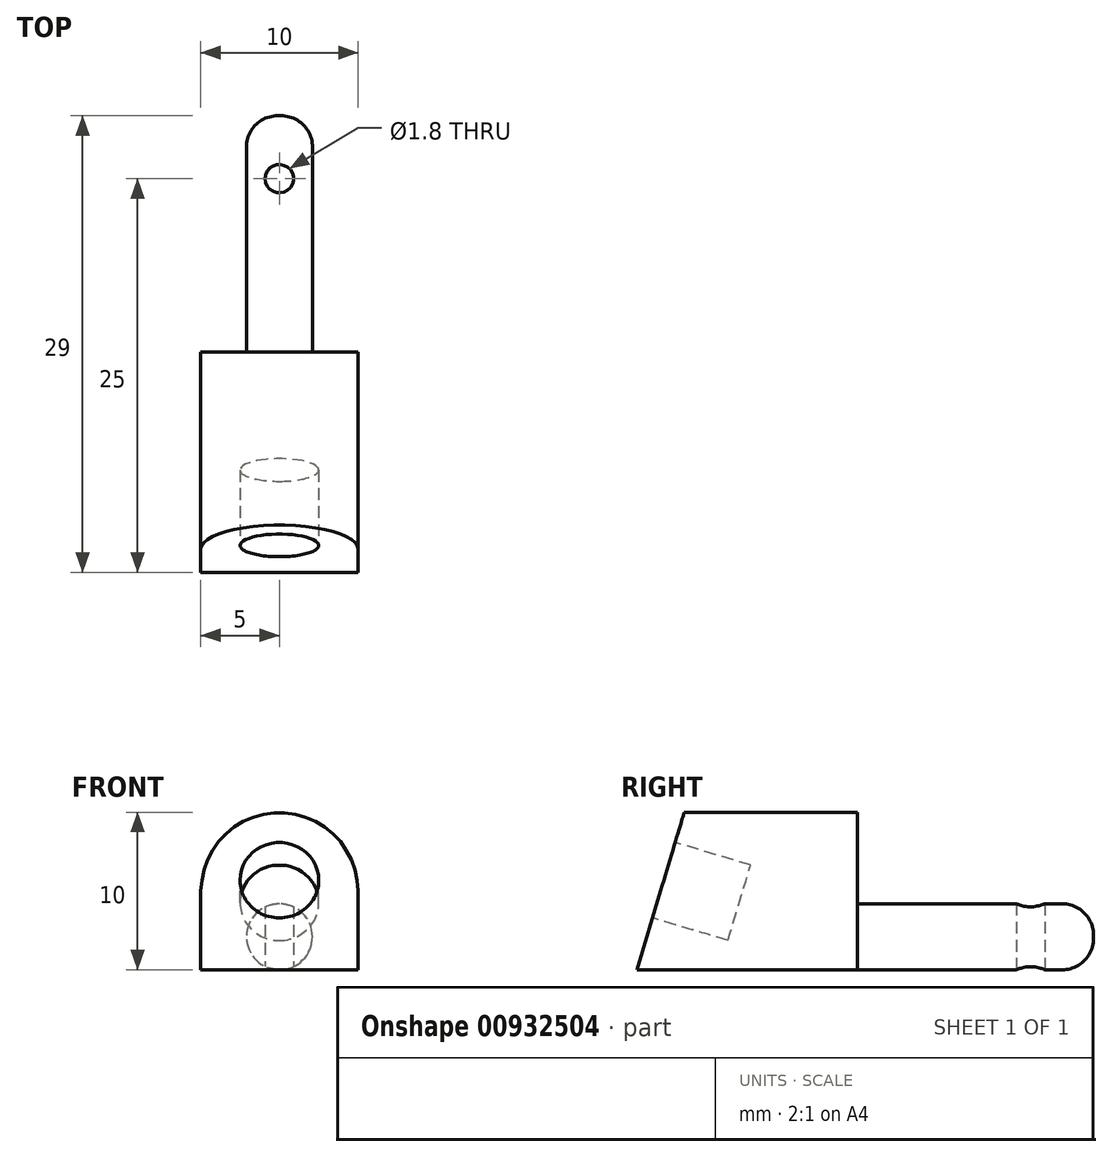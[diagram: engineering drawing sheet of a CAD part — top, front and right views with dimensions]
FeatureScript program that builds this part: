
annotation { "Feature Type Name" : "Feature", "Feature Type Description" : "" }
export const myFeature = defineFeature(function(context is Context, id is Id, definition is map)
    precondition{}
    {
        {
            var Q0;
            Q0=qCreatedBy(makeId("Top.planeOp"),FACE);
            var sketch = newSketch(context, id + "F0", { "sketchPlane" : qUnion([Q0])});
            skLineSegment(sketch, "E0.bottom", {"start": v(5, 7) * mm, "end": v(-5, 7) * mm});
            skLineSegment(sketch, "E0.top", {"start": v(5, -7) * mm, "end": v(-5, -7) * mm});
            skLineSegment(sketch, "E0.left", {"start": v(5, 7) * mm, "end": v(5, -7) * mm});
            skLineSegment(sketch, "E0.right", {"start": v(-5, 7) * mm, "end": v(-5, -7) * mm});
            skPoint(sketch, "E0.middle", {"position": v(0, 0) * mm});
            skSolve(sketch);
        }
        {
            var Q0;
            Q0 = qSketchRegion(id + "F0", true);
            extrude(context, id + "F1", {"entities" : qUnion([Q0]), "depth" : 10 * mm, "offsetDistance" : 25 * mm});
        }
        {
            var Q0;
            Q0=makeQuery(id+"F1.opExtrude","SWEPT_FACE",FACE,{"disambiguationData":[OSD([sQuery(id+"F0.wireOp",EDGE,"E0.bottom")])]});
            var sketch = newSketch(context, id + "F2", { "sketchPlane" : qUnion([Q0])});
            skCircle(sketch, "E1", {"center": v(0, 2.1) * mm, "radius": 2.1 * mm});
            skSolve(sketch);
        }
        {
            var Q0;
            Q0 = qSketchRegion(id + "F2", true);
            extrude(context, id + "F3", {"entities" : qUnion([Q0]), "operationType" : NewBodyOperationType.ADD, "depth" : 15 * mm, "offsetDistance" : 25 * mm});
        }
        {
            var Q0;
            Q0=qCreatedBy(makeId("Top.planeOp"),FACE);
            var sketch = newSketch(context, id + "F4", { "sketchPlane" : qUnion([Q0])});
            skCircle(sketch, "E2", {"center": v(0, 18) * mm, "radius": 0.9 * mm});
            skSolve(sketch);
        }
        {
            var Q0;
            Q0 = qSketchRegion(id + "F4", true);
            extrude(context, id + "F5", {"entities" : qUnion([Q0]), "operationType" : NewBodyOperationType.REMOVE, "depth" : 5 * mm, "offsetDistance" : 25 * mm});
        }
        {
            var Q0;
            Q0=makeQuery(id+"F3.opExtrude","CAP_EDGE",EDGE,{"disambiguationData":[OSD([sQuery(id+"F2.wireOp",EDGE,"E1")])],"isStart":false});
            fillet(context, id + "F6", {"entities" : qUnion([Q0]), "radius" : 2 * mm, "tangentPropagation" : true, "allowEdgeOverflow" : false});
        }
        {
            var Q0;
            Q0=makeQuery(id+"F1.opExtrude","SWEPT_FACE",FACE,{"disambiguationData":[OSD([sQuery(id+"F0.wireOp",EDGE,"E0.right")])]});
            var sketch = newSketch(context, id + "F7", { "sketchPlane" : qUnion([Q0])});
            skLineSegment(sketch, "E3", {"start": v(7, 0) * mm, "end": v(4, 10) * mm});
            skLineSegment(sketch, "E4", {"start": v(4, 10) * mm, "end": v(7, 10) * mm});
            skLineSegment(sketch, "E5", {"start": v(7, 10) * mm, "end": v(7, 0) * mm});
            skSolve(sketch);
        }
        {
            var Q0;
            Q0 = qSketchRegion(id + "F7", true);
            extrude(context, id + "F8", {"entities" : qUnion([Q0]), "operationType" : NewBodyOperationType.REMOVE, "oppositeDirection" : true, "depth" : 10 * mm, "offsetDistance" : 25 * mm});
        }
        {
            var Q0;
            Q0=makeQuery(id+"F8.boolean.opBoolean","COPY",FACE,{"derivedFrom":makeQuery(id+"F8.opExtrude","SWEPT_FACE",FACE,{"disambiguationData":[OSD([sQuery(id+"F7.wireOp",EDGE,"E3")])]})});
            var sketch = newSketch(context, id + "F9", { "sketchPlane" : qUnion([Q0])});
            skCircle(sketch, "E6", {"center": v(0, 3.93) * mm, "radius": 2.5 * mm});
            skSolve(sketch);
        }
        {
            var Q0;
            Q0 = qSketchRegion(id + "F9", true);
            extrude(context, id + "F10", {"entities" : qUnion([Q0]), "operationType" : NewBodyOperationType.REMOVE, "oppositeDirection" : true, "depth" : 5 * mm, "offsetDistance" : 25 * mm});
        }
        {
            var Q0;
            Q0=makeQuery(id+"F1.opExtrude","CAP_EDGE",EDGE,{"disambiguationData":[OSD([sQuery(id+"F0.wireOp",EDGE,"E0.right")])],"isStart":false});
            var Q1;
            Q1=makeQuery(id+"F1.opExtrude","CAP_EDGE",EDGE,{"disambiguationData":[OSD([sQuery(id+"F0.wireOp",EDGE,"E0.left")])],"isStart":false});
            fillet(context, id + "F11", {"entities" : qUnion([Q0, Q1]), "radius" : 5 * mm, "tangentPropagation" : true, "allowEdgeOverflow" : false});
        }
    });
